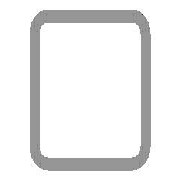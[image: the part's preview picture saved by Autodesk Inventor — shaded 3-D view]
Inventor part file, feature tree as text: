
AUTODESK INVENTOR PART (.ipt)
format: ipt  version: 2025.4 (Build 294407000, 407)  size: 152,576 bytes
history: native  units: mm (DEFAULTED — no unit token found)
features: other x3, sketch x2, extrude x1, plane x1
ambient origin geometry x8: Origin, YZ Plane, XZ Plane, XY Plane, X Axis, Y Axis, Z Axis, Center Point
bodies: Solid1 (feature_tree), Body (feature_tree)
feature tree (7):
  other  "Driven Length"
  other  "Start plane"
  other  "End plane"
  extrude  "Extrusion3"  TaperAngle=0.0deg  [1 undecoded]
  sketch  "Sketch3"  dims[d3=1000.0mm d4=0.0mm]
  plane  "Work Plane3"
  sketch  "Sketch7"  dims[d7=6.0mm d9=80.0mm d11=80.0mm d12=3.0mm d13=-0.0mm d14=1000.0mm d15=40.0mm d16=40.0mm d17=90.0deg d18=1000.0mm d37=280.0mm d38=11.34464mm d39=0.0mm d40=0.0mm]
note: 1 required parameter value undecoded (feature->parameter linkage not recoverable at this tier; creation-order binding heuristic only, values carry confidence <= 0.55)
